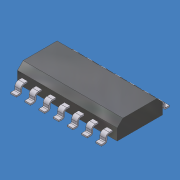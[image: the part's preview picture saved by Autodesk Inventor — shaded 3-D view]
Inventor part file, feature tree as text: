
AUTODESK INVENTOR PART (.ipt)
format: ipt  version: 2012 (Build 160160000, 160)  size: 246,784 bytes
history: native  units: mm (DEFAULTED — no unit token found)
features: sketch x3, extrude x1, chamfer x1, plane x1, sweep x1, mirror x1, pattern_linear x1
ambient origin geometry x8: Origin, YZ Plane, XZ Plane, XY Plane, X Axis, Y Axis, Z Axis, Center Point
bodies: Solid1 (feature_tree)
feature tree (9):
  extrude  "Extrusion1"  Depth=8.8mm
  chamfer  "Chamfer1"  Distance=1.5mm
  sketch  "Sketch2"  dims[d4=0.5mm d5=2.0mm d6=0.5mm]
  plane  "Work Plane3"
  sweep  "Sweep1"
  mirror  "Mirror1"
  pattern_linear  "Rectangular Pattern1"  Spacing1=0.4mm  [1 undecoded]
  sketch  "Sketch1"  dims[d0=4.0mm d1=8.8mm d2=1.5mm d3=0.0mm]
  sketch  "Sketch3"  dims[d7=0.125mm d8=0.4mm d9=0.5mm d10=90.0deg d11=0.5mm d12=0.6mm d13=0.5mm d14=0.2mm d15=0.0mm d16=70.0mm d18=1.25mm d19=45.0deg]
note: 1 required parameter value undecoded (feature->parameter linkage not recoverable at this tier; creation-order binding heuristic only, values carry confidence <= 0.55)
